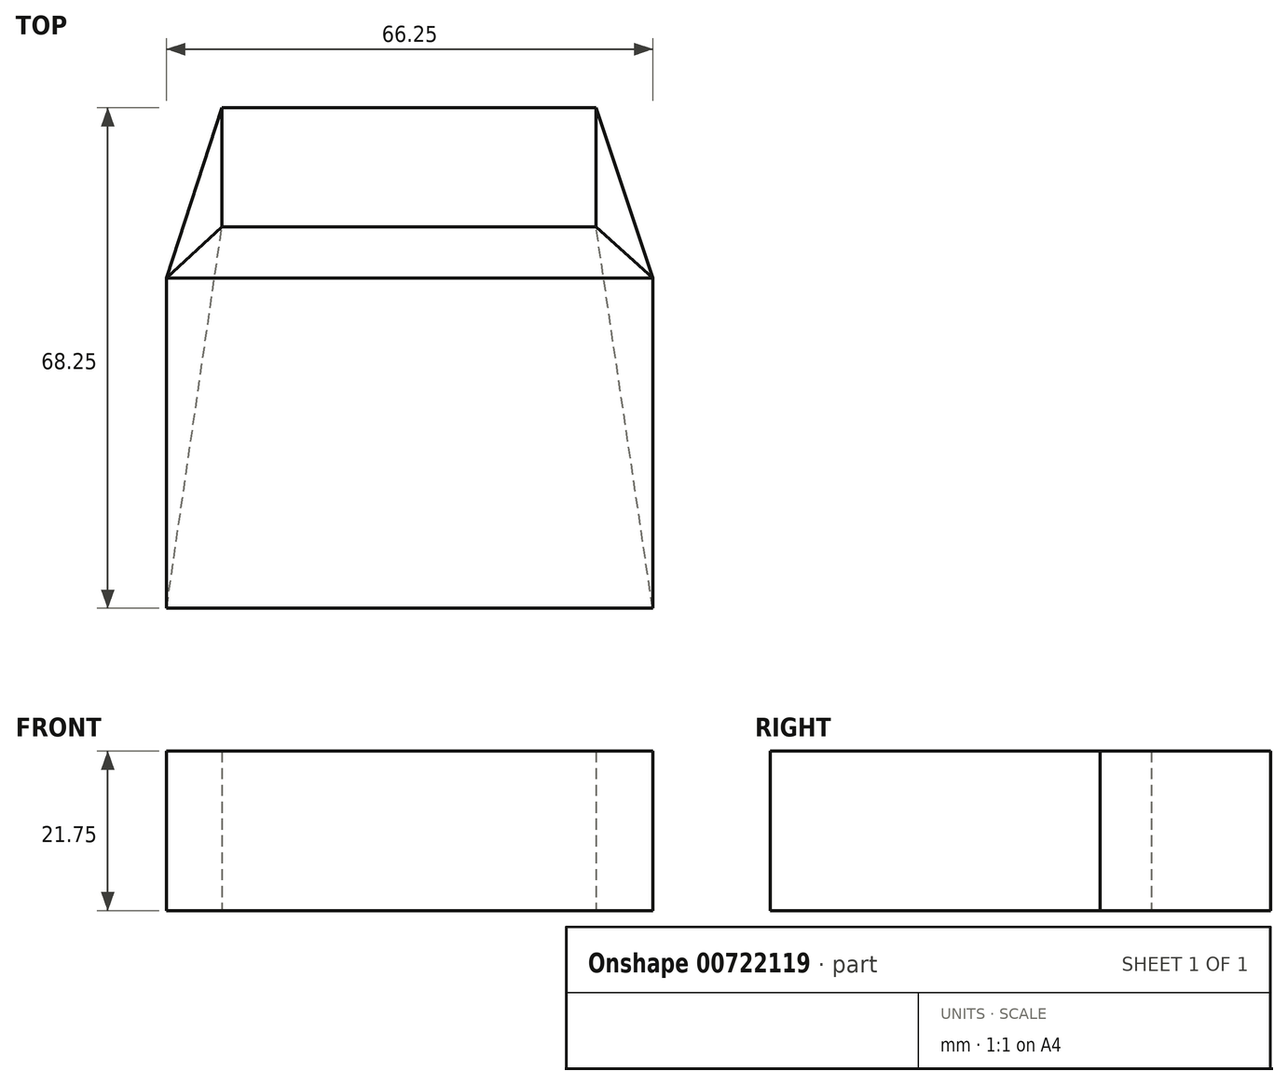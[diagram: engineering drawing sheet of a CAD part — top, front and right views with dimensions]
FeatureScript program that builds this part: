
annotation { "Feature Type Name" : "Feature", "Feature Type Description" : "" }
export const myFeature = defineFeature(function(context is Context, id is Id, definition is map)
    precondition{}
    {
        {
            var Q0;
            Q0=qCreatedBy(makeId("Top.planeOp"),FACE);
            var sketch = newSketch(context, id + "F0", { "sketchPlane" : qUnion([Q0])});
            skLineSegment(sketch, "E0.bottom", {"start": v(-40.16, 3.94) * mm, "end": v(26.1, 3.94) * mm});
            skLineSegment(sketch, "E0.top", {"start": v(-40.16, -41.06) * mm, "end": v(26.1, -41.06) * mm});
            skLineSegment(sketch, "E0.left", {"start": v(-40.16, 3.94) * mm, "end": v(-40.16, -41.06) * mm});
            skLineSegment(sketch, "E0.right", {"start": v(26.1, 3.94) * mm, "end": v(26.1, -41.06) * mm});
            skSolve(sketch);
        }
        {
            var Q0;
            Q0=makeQuery(id+"F0.imprint","IMPRINT",FACE,{"disambiguationData":[TD([[makeQuery(id+"F0.imprint","IMPRINT",EDGE,{"derivedFrom":sQuery(id+"F0.wireOp",EDGE,"E0.bottom")}),-1.0]])]});
            extrude(context, id + "F1", {"entities" : qUnion([Q0]), "depth" : 21.75 * mm, "offsetDistance" : 25.4 * mm});
        }
        {
            var Q0;
            Q0=qCreatedBy(makeId("Top.planeOp"),FACE);
            var sketch = newSketch(context, id + "F2", { "sketchPlane" : qUnion([Q0])});
            skLineSegment(sketch, "E1.bottom", {"start": v(-32.62, 10.94) * mm, "end": v(18.38, 10.94) * mm});
            skLineSegment(sketch, "E1.top", {"start": v(-32.62, 27.2) * mm, "end": v(18.38, 27.2) * mm});
            skLineSegment(sketch, "E1.left", {"start": v(-32.62, 10.94) * mm, "end": v(-32.62, 27.2) * mm});
            skLineSegment(sketch, "E1.right", {"start": v(18.38, 10.94) * mm, "end": v(18.38, 27.2) * mm});
            skPoint(sketch, "E1.middle", {"position": v(0, 0) * mm});
            skSolve(sketch);
        }
        {
            var Q0;
            Q0 = qSketchRegion(id + "F2", true);
            extrude(context, id + "F3", {"entities" : qUnion([Q0]), "depth" : 21.74 * mm, "offsetDistance" : 25.4 * mm});
        }
        {
            var Q0;
            Q0=makeQuery(id+"F1.opExtrude","SWEPT_FACE",FACE,{"disambiguationData":[OSD([sQuery(id+"F0.wireOp",EDGE,"E0.left")])]});
            var Q1;
            Q1=makeQuery(id+"F3.opExtrude","SWEPT_FACE",FACE,{"disambiguationData":[OSD([sQuery(id+"F2.wireOp",EDGE,"E1.left")])]});
            loft(context, id + "F4", {"sheetProfilesArray" : [{ "sheetProfileEntities" : qUnion([Q0]) }, { "sheetProfileEntities" : qUnion([Q1]) }]});
        }
        {
            var Q0;
            Q0=makeQuery(id+"F1.opExtrude","SWEPT_FACE",FACE,{"disambiguationData":[OSD([sQuery(id+"F0.wireOp",EDGE,"E0.right")])]});
            var Q1;
            Q1=makeQuery(id+"F3.opExtrude","SWEPT_FACE",FACE,{"disambiguationData":[OSD([sQuery(id+"F2.wireOp",EDGE,"E1.right")])]});
            loft(context, id + "F5", {"sheetProfilesArray" : [{ "sheetProfileEntities" : qUnion([Q0]) }, { "sheetProfileEntities" : qUnion([Q1]) }]});
        }
        {
            var Q0;
            Q0=makeQuery(id+"F3.opExtrude","SWEPT_FACE",FACE,{"disambiguationData":[OSD([sQuery(id+"F2.wireOp",EDGE,"E1.bottom")])]});
            var Q1;
            Q1=makeQuery(id+"F1.opExtrude","SWEPT_FACE",FACE,{"disambiguationData":[OSD([sQuery(id+"F0.wireOp",EDGE,"E0.bottom")])]});
            loft(context, id + "F6", {"sheetProfilesArray" : [{ "sheetProfileEntities" : qUnion([Q0]) }, { "sheetProfileEntities" : qUnion([Q1]) }]});
        }
    });
